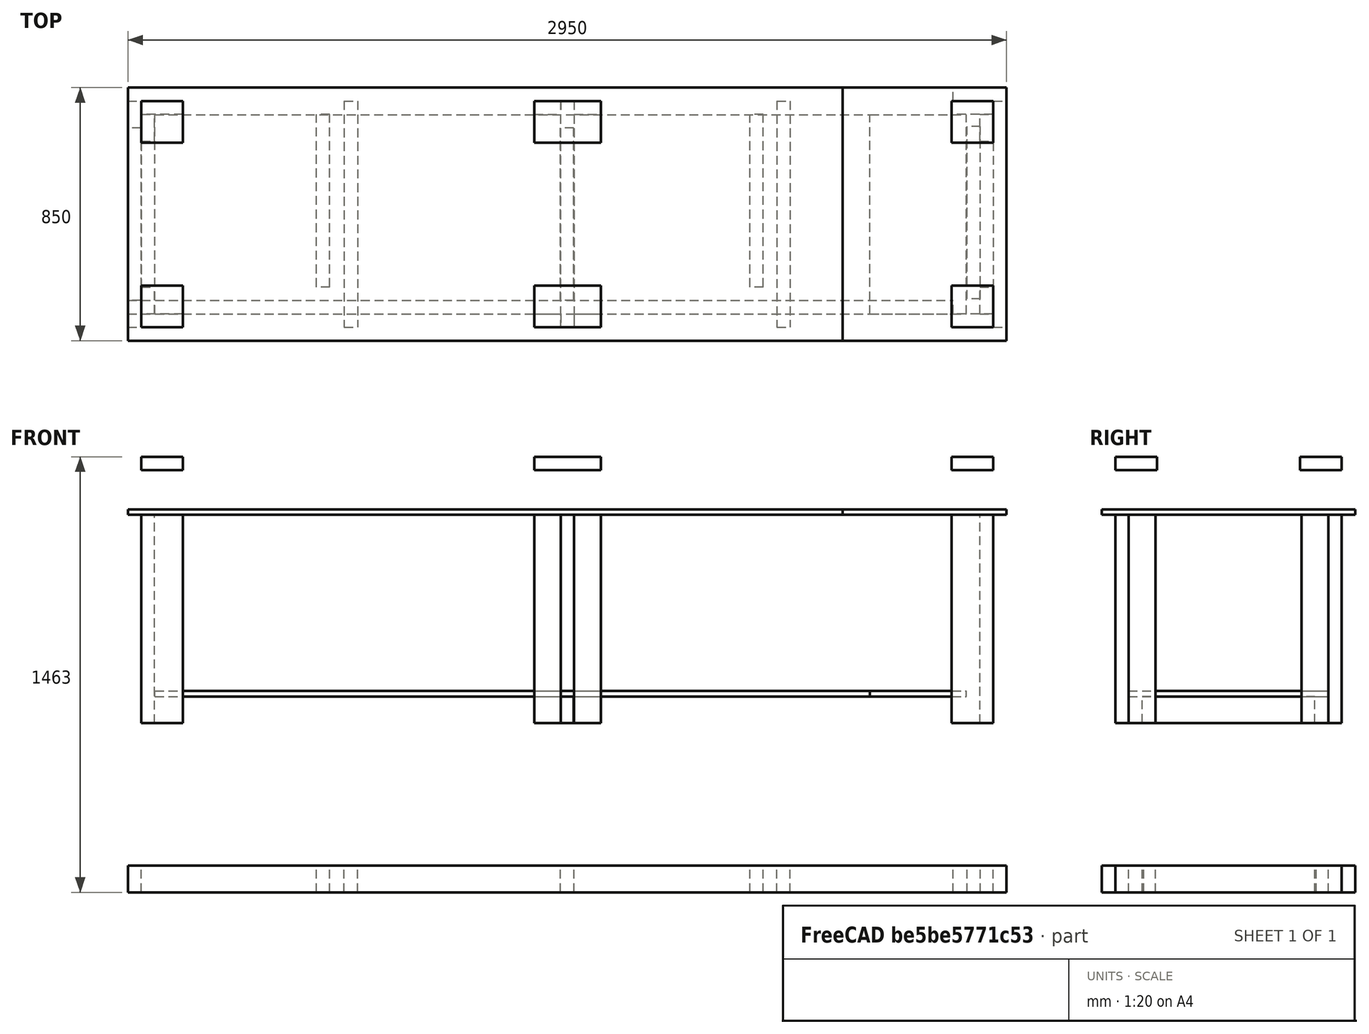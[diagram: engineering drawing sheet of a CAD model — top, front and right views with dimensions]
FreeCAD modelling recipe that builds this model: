
FCSTD DOCUMENT  (FreeCAD 0.19R24291 (Git))
Label: Workbench
License: All rights reserved
LicenseURL: http://en.wikipedia.org/wiki/All_rights_reserved
objects: Part::Box×36, App::Link×35, App::LinkGroup×6
note: 36 computed .brp shape members not serialized (recipe doc carries the construction recipe); baked Part::Feature solids carry a one-line shape summary decoded from their .brp

FEATURE [Part::Box] Box001  label="45x90x2950 TOP1"
  AttacherType = Attacher::AttachEngine3D
  Height = 90
  Length = 2950
  Placement = pos=(0,-805,0) rot=(0,0,1;0rad)
  Width = 45
FEATURE [Part::Box] Box002  label="45x90x2950 TOP2"
  AttacherType = Attacher::AttachEngine3D
  Height = 90
  Length = 2950
  Width = 45
FEATURE [Part::Box] Box  label="45x90x760 TOP1"
  AttacherType = Attacher::AttachEngine3D
  Height = 90
  Length = 760
  Placement = pos=(0,0,0) rot=(0,0,-1;1.5708rad)
  Width = 45
FEATURE [Part::Box] Box003  label="45x90x760 TOP2"
  AttacherType = Attacher::AttachEngine3D
  Height = 90
  Length = 760
  Placement = pos=(2905,0,0) rot=(0,0,-1;1.5708rad)
  Width = 45
FEATURE [Part::Box] Box004  label="45x90x760 TOP003"
  AttacherType = Attacher::AttachEngine3D
  Height = 90
  Length = 760
  Placement = pos=(1452.5,0,0) rot=(0,0,-1;1.5708rad)
  Width = 45
FEATURE [Part::Box] Box005  label="45x90x760 TOP004"
  AttacherType = Attacher::AttachEngine3D
  Height = 90
  Length = 760
  Placement = pos=(726.25,0,0) rot=(0,0,-1;1.5708rad)
  Width = 45
FEATURE [Part::Box] Box006  label="45x90x760 TOP005"
  AttacherType = Attacher::AttachEngine3D
  Height = 90
  Length = 760
  Placement = pos=(2178.5,0,0) rot=(0,0,-1;1.5708rad)
  Width = 45
FEATURE [Part::Box] Box007  label="45x90x2860 BASE001"
  AttacherType = Attacher::AttachEngine3D
  Height = 90
  Length = 2770
  Width = 45
FEATURE [Part::Box] Box008  label="45x90x2860 BASE002"
  AttacherType = Attacher::AttachEngine3D
  Height = 90
  Length = 2770
  Placement = pos=(0,-715,0) rot=(0,0,1;0rad)
  Width = 45
FEATURE [Part::Box] Box009  label="45x90x670 BASE001"
  AttacherType = Attacher::AttachEngine3D
  Height = 90
  Length = 580
  Placement = pos=(45,-670,0) rot=(0,0,1;1.5708rad)
  Width = 45
FEATURE [Part::Box] Box010  label="45x90x670 BASE002"
  AttacherType = Attacher::AttachEngine3D
  Height = 90
  Length = 580
  Placement = pos=(2862,-665,0) rot=(0,0,1;1.5708rad)
  Width = 45
FEATURE [Part::Box] Box011  label="45x90x670 BASE003"
  AttacherType = Attacher::AttachEngine3D
  Height = 90
  Length = 580
  Placement = pos=(678,-625,0) rot=(0,0,1;1.5708rad)
  Width = 45
FEATURE [Part::Box] Box012  label="45x90x670 BASE004"
  AttacherType = Attacher::AttachEngine3D
  Height = 90
  Length = 580
  Placement = pos=(2133,-625,0) rot=(0,0,1;1.5708rad)
  Width = 45
FEATURE [App::Link] Link  label="45x90x580 BASE005"
  LinkTransform = true
  LinkedObject = -> Box012
FEATURE [App::Link] Link001  label="45x90x2770 BASE003"
  LinkPlacement = pos=(45,-45,-3.05176e-05) rot=(0,0,1;0rad)
  LinkTransform = true
  LinkedObject = -> Box007
  Placement = pos=(45,-45,-3.05176e-05) rot=(0,0,1;0rad)
FEATURE [App::Link] Link002  label="45x90x2770 BASE004"
  LinkPlacement = pos=(45,45.0009,0) rot=(0,0,1;0rad)
  LinkTransform = true
  LinkedObject = -> Box008
  Placement = pos=(45,45.0009,0) rot=(0,0,1;0rad)
FEATURE [App::Link] Link003  label="45x90x580 BASE006"
  LinkPlacement = pos=(44.9998,44.9998,-9.15527e-05) rot=(0,0,1;0rad)
  LinkTransform = true
  LinkedObject = -> Box009
  Placement = pos=(44.9998,44.9998,-9.15527e-05) rot=(0,0,1;0rad)
FEATURE [App::Link] Link004  label="45x90x580 BASE007"
  LinkPlacement = pos=(-47.0026,40.0039,-0.000183105) rot=(0,0,1;0rad)
  LinkTransform = true
  LinkedObject = -> Box010
  Placement = pos=(-47.0026,40.0039,-0.000183105) rot=(0,0,1;0rad)
FEATURE [App::Link] Link005  label="45x90x580 BASE008"
  LinkPlacement = pos=(93.0004,-0.00065788,-6.10352e-05) rot=(0,0,1;0rad)
  LinkTransform = true
  LinkedObject = -> Box011
  Placement = pos=(93.0004,-0.00065788,-6.10352e-05) rot=(0,0,1;0rad)
FEATURE [App::LinkGroup] LinkGroup
  ElementList = -> [Link,Link001,Link002,Link003,Link004,Link005]
  LinkMode = 1
  Placement = pos=(45.0002,-45.0002,568) rot=(0,0,1;0rad)
FEATURE [App::Link] Link006  label="45x90x760 TOP006"
  LinkTransform = true
  LinkedObject = -> Box006
FEATURE [App::Link] Link007  label="45x90x2950 TOP003"
  LinkTransform = true
  LinkedObject = -> Box001
FEATURE [App::Link] Link008  label="45x90x2950 TOP004"
  LinkTransform = true
  LinkedObject = -> Box002
FEATURE [App::Link] Link009  label="45x90x760 TOP007"
  LinkTransform = true
  LinkedObject = -> Box
FEATURE [App::Link] Link010  label="45x90x760 TOP008"
  LinkTransform = true
  LinkedObject = -> Box003
FEATURE [App::Link] Link011  label="45x90x760 TOP009"
  LinkTransform = true
  LinkedObject = -> Box004
FEATURE [App::Link] Link012  label="45x90x760 TOP010"
  LinkTransform = true
  LinkedObject = -> Box005
FEATURE [App::LinkGroup] LinkGroup001
  ElementList = -> [Link006,Link007,Link008,Link009,Link010,Link011,Link012]
  LinkMode = 1
  Placement = pos=(-7.67708e-05,-0.000244141,1178) rot=(0,0,1;0rad)
FEATURE [Part::Box] Box013  label="45x140x700 LEG001"
  AttacherType = Attacher::AttachEngine3D
  Height = 140
  Length = 700
  Placement = pos=(185,-45,568) rot=(0,-1,0;1.5708rad)
  Width = 45
FEATURE [Part::Box] Box014  label="45x140x700 LEG002"
  AttacherType = Attacher::AttachEngine3D
  Height = 140
  Length = 700
  Placement = pos=(185,-760,568) rot=(0,-1,0;1.5708rad)
  Width = 45
FEATURE [Part::Box] Box015  label="45x140x700 LEG003"
  AttacherType = Attacher::AttachEngine3D
  Height = 140
  Length = 700
  Placement = pos=(2905,-45,568) rot=(0,-1,0;1.5708rad)
  Width = 45
FEATURE [Part::Box] Box016  label="45x140x700 LEG004"
  AttacherType = Attacher::AttachEngine3D
  Height = 140
  Length = 700
  Placement = pos=(2905,-760,568) rot=(0,-1,0;1.5708rad)
  Width = 45
FEATURE [Part::Box] Box017  label="45x90x700 LEG001"
  AttacherType = Attacher::AttachEngine3D
  Height = 90
  Length = 700
  Placement = pos=(2860,-715,568) rot=(0.57735,0.57735,0.57735;4.18879rad)
  Width = 45
FEATURE [Part::Box] Box018  label="45x90x700 LEG002"
  AttacherType = Attacher::AttachEngine3D
  Height = 90
  Length = 700
  Placement = pos=(2860,-135,568) rot=(0.57735,0.57735,0.57735;4.18879rad)
  Width = 45
FEATURE [Part::Box] Box019  label="45x90x700 LEG003"
  AttacherType = Attacher::AttachEngine3D
  Height = 90
  Length = 700
  Placement = pos=(45,-135,568) rot=(0.57735,0.57735,0.57735;4.18879rad)
  Width = 45
FEATURE [Part::Box] Box020  label="45x90x700 LEG004"
  AttacherType = Attacher::AttachEngine3D
  Height = 90
  Length = 700
  Placement = pos=(45,-715,568) rot=(0.57735,0.57735,0.57735;4.18879rad)
  Width = 45
FEATURE [Part::Box] Box021  label="45x90x700 LEG005"
  AttacherType = Attacher::AttachEngine3D
  Height = 90
  Length = 700
  Placement = pos=(1364,-715,568) rot=(0.707107,0,0.707107;3.14159rad)
  Width = 45
FEATURE [Part::Box] Box022  label="45x90x700 LEG006"
  AttacherType = Attacher::AttachEngine3D
  Height = 90
  Length = 700
  Placement = pos=(1498,-715,568) rot=(0.707107,0,0.707107;3.14159rad)
  Width = 45
FEATURE [Part::Box] Box023  label="45x90x700 LEG007"
  AttacherType = Attacher::AttachEngine3D
  Height = 90
  Length = 700
  Placement = pos=(1364,0,568) rot=(0.707107,0,0.707107;3.14159rad)
  Width = 45
FEATURE [Part::Box] Box024  label="45x90x700 LEG008"
  AttacherType = Attacher::AttachEngine3D
  Height = 90
  Length = 700
  Placement = pos=(1498,0,568) rot=(0.707107,0,0.707107;3.14159rad)
  Width = 45
FEATURE [Part::Box] Box025  label="18x1200x550 MDF002"
  AttacherType = Attacher::AttachEngine3D
  Height = 18
  Length = 550
  Placement = pos=(2400,-805,1268) rot=(0,0,1;0rad)
  Width = 850
FEATURE [Part::Box] Box026  label="18x1200x2400 MDF001"
  AttacherType = Attacher::AttachEngine3D
  Height = 18
  Length = 2400
  Placement = pos=(0,-805,1268) rot=(0,0,1;0rad)
  Width = 850
FEATURE [Part::Box] Box027  label="18x670x2400 MDF003"
  AttacherType = Attacher::AttachEngine3D
  Height = 18
  Length = 2400
  Placement = pos=(91,-716,658) rot=(0,0,1;0rad)
  Width = 670
FEATURE [Part::Box] Box028  label="18x670x279 MDF004"
  AttacherType = Attacher::AttachEngine3D
  Height = 18
  Length = 324
  Placement = pos=(2491,-716,658) rot=(0,0,1;0rad)
  Width = 670
FEATURE [Part::Box] Box029  label="45x140x140 FOOT001"
  AttacherType = Attacher::AttachEngine3D
  Height = 45
  Length = 140
  Placement = pos=(45,-140,1418) rot=(0,0,1;0rad)
  Width = 140
FEATURE [Part::Box] Box030  label="45x140x140 FOOT002"
  AttacherType = Attacher::AttachEngine3D
  Height = 45
  Length = 140
  Placement = pos=(45,-760,1418) rot=(0,0,1;0rad)
  Width = 140
FEATURE [Part::Box] Box031  label="45x140x140 FOOT003"
  AttacherType = Attacher::AttachEngine3D
  Height = 45
  Length = 140
  Placement = pos=(2765,-140,1418) rot=(0,0,1;0rad)
  Width = 140
FEATURE [Part::Box] Box032  label="45x140x140 FOOT004"
  AttacherType = Attacher::AttachEngine3D
  Height = 45
  Length = 140
  Placement = pos=(2765,-760,1418) rot=(0,0,1;0rad)
  Width = 140
FEATURE [Part::Box] Box033  label="45x140x224 FOOT005"
  AttacherType = Attacher::AttachEngine3D
  Height = 45
  Length = 224
  Placement = pos=(1364,-760,1418) rot=(0,0,1;0rad)
  Width = 140
FEATURE [Part::Box] Box034  label="45x140x224 FOOT006"
  AttacherType = Attacher::AttachEngine3D
  Height = 45
  Length = 224
  Placement = pos=(1364,-140,1418) rot=(0,0,1;0rad)
  Width = 140
FEATURE [App::Link] Link025  label="45x140x140 FOOT005"
  LinkTransform = true
  LinkedObject = -> Box029
FEATURE [App::Link] Link026  label="45x140x140 FOOT006"
  LinkTransform = true
  LinkedObject = -> Box030
FEATURE [App::Link] Link027  label="45x140x140 FOOT007"
  LinkTransform = true
  LinkedObject = -> Box031
FEATURE [App::Link] Link028  label="45x140x140 FOOT008"
  LinkTransform = true
  LinkedObject = -> Box032
FEATURE [App::Link] Link029  label="45x140x224 FOOT007"
  LinkTransform = true
  LinkedObject = -> Box033
FEATURE [App::Link] Link030  label="45x140x224 FOOT008"
  LinkTransform = true
  LinkedObject = -> Box034
FEATURE [App::LinkGroup] LinkGroup003
  ElementList = -> [Link025,Link026,Link027,Link028,Link029,Link030]
  LinkMode = 1
  Placement = pos=(-0.00012207,0.00012207,-895) rot=(0,0,1;0rad)
FEATURE [App::Link] Link031  label="45x90x700 LEG009"
  LinkTransform = true
  LinkedObject = -> Box024
FEATURE [App::Link] Link032  label="45x140x700 LEG005"
  LinkTransform = true
  LinkedObject = -> Box013
FEATURE [App::Link] Link033  label="45x140x700 LEG006"
  LinkTransform = true
  LinkedObject = -> Box014
FEATURE [App::Link] Link034  label="45x140x700 LEG007"
  LinkTransform = true
  LinkedObject = -> Box015
FEATURE [App::Link] Link035  label="45x140x700 LEG008"
  LinkTransform = true
  LinkedObject = -> Box016
FEATURE [App::Link] Link036  label="45x90x700 LEG010"
  LinkTransform = true
  LinkedObject = -> Box017
FEATURE [App::Link] Link037  label="45x90x700 LEG011"
  LinkTransform = true
  LinkedObject = -> Box018
FEATURE [App::Link] Link038  label="45x90x700 LEG012"
  LinkTransform = true
  LinkedObject = -> Box019
FEATURE [App::Link] Link039  label="45x90x700 LEG013"
  LinkTransform = true
  LinkedObject = -> Box020
FEATURE [App::Link] Link040  label="45x90x700 LEG014"
  LinkTransform = true
  LinkedObject = -> Box021
FEATURE [App::Link] Link041  label="45x90x700 LEG015"
  LinkTransform = true
  LinkedObject = -> Box022
FEATURE [App::Link] Link042  label="45x90x700 LEG016"
  LinkTransform = true
  LinkedObject = -> Box023
FEATURE [App::LinkGroup] LinkGroup004
  ElementList = -> [Link031,Link032,Link033,Link034,Link035,Link036,Link037,Link038,Link039,Link040,Link041,Link042]
  LinkMode = 1
FEATURE [App::Link] Link043  label="18x1200x550 MDF003"
  LinkTransform = true
  LinkedObject = -> Box025
FEATURE [App::Link] Link044  label="18x1200x2400 MDF002"
  LinkTransform = true
  LinkedObject = -> Box026
FEATURE [App::LinkGroup] LinkGroup005
  ElementList = -> [Link043,Link044]
  LinkMode = 1
FEATURE [App::Link] Link045  label="18x670x279 MDF005"
  LinkTransform = true
  LinkedObject = -> Box028
FEATURE [App::Link] Link046  label="18x670x2400 MDF004"
  LinkTransform = true
  LinkedObject = -> Box027
FEATURE [App::LinkGroup] LinkGroup006
  ElementList = -> [Link045,Link046]
  LinkMode = 1
FEATURE [Part::Box] Box035  label="45x90x670 BASE005"
  AttacherType = Attacher::AttachEngine3D
  Height = 90
  Length = 580
  Placement = pos=(1497,-670,569) rot=(0,0,1;1.5708rad)
  Width = 45
